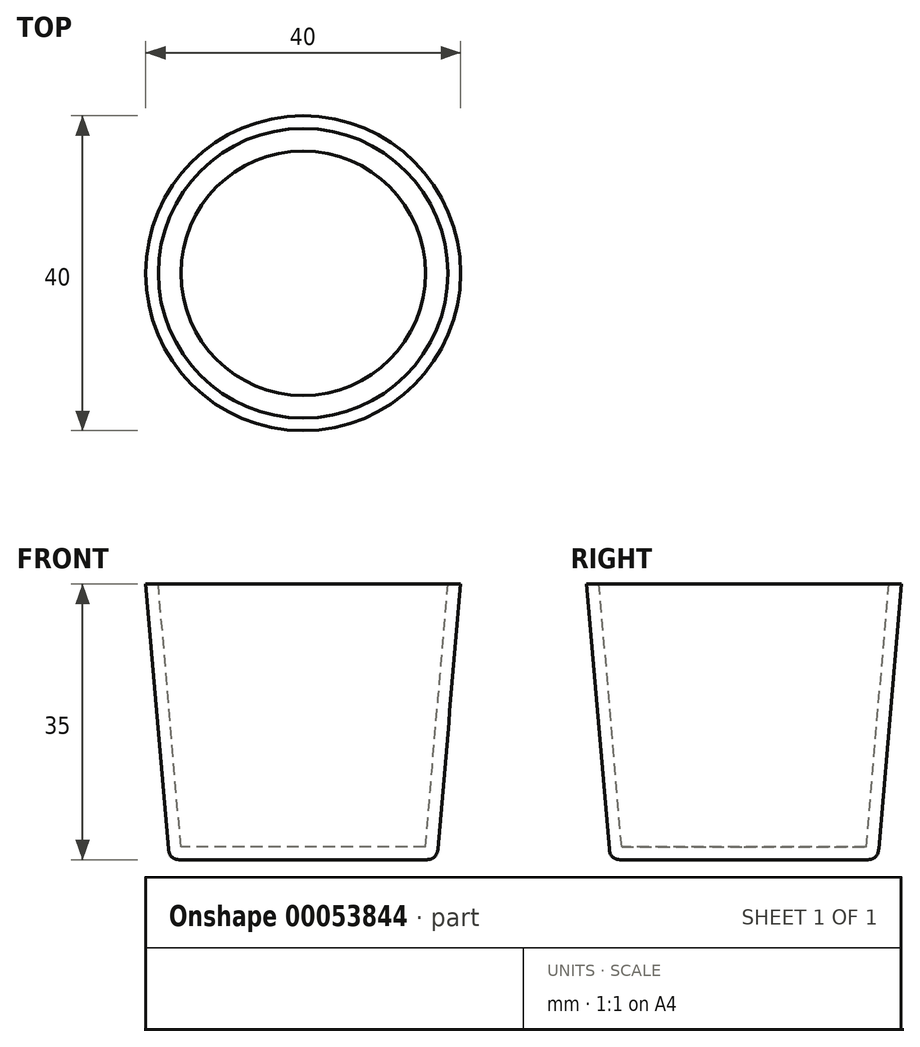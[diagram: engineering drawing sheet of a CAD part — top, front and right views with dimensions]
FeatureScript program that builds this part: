
annotation { "Feature Type Name" : "Feature", "Feature Type Description" : "" }
export const myFeature = defineFeature(function(context is Context, id is Id, definition is map)
    precondition{}
    {
        {
            var Q0;
            Q0=qCreatedBy(makeId("Front.planeOp"),FACE);
            var sketch = newSketch(context, id + "F0", { "sketchPlane" : qUnion([Q0])});
            skLineSegment(sketch, "E0", {"start": v(0, 0) * mm, "end": v(17, 0) * mm});
            skLineSegment(sketch, "E1", {"start": v(17, 0) * mm, "end": v(20, 35) * mm});
            skLineSegment(sketch, "E2", {"start": v(20, 35) * mm, "end": v(0, 35) * mm});
            skLineSegment(sketch, "E3", {"start": v(0, 35) * mm, "end": v(0, 0) * mm});
            skSolve(sketch);
        }
        {
            var Q0;
            Q0=makeQuery(id+"F0.imprint","IMPRINT",FACE,{"disambiguationData":[TD([[makeQuery(id+"F0.imprint","IMPRINT",EDGE,{"derivedFrom":sQuery(id+"F0.wireOp",EDGE,"E0")}),1.0]])]});
            var Q1;
            Q1=sQuery(id+"F0.wireOp",EDGE,"E3");
            revolve(context, id + "F1", {"entities" : qUnion([Q0]), "axis" : qUnion([Q1]), "revolveType" : RevolveType.FULL});
        }
        {
            var Q0;
            Q0=makeQuery(id+"F1.opRevolve","SWEPT_FACE",FACE,{"disambiguationData":[OSD([sQuery(id+"F0.wireOp",EDGE,"E2")])]});
            shell(context, id + "F2", {"entities" : qUnion([Q0]), "thickness" : 1.6 * mm});
        }
        {
            var Q0;
            Q0=makeQuery(id+"F1.opRevolve","SWEPT_EDGE",EDGE,{"disambiguationData":[OSD([sQuery(id+"F0.wireOp",EDGE,"E0"),sQuery(id+"F0.wireOp",EDGE,"E1")])]});
            fillet(context, id + "F3", {"entities" : qUnion([Q0]), "radius" : 1.5 * mm, "tangentPropagation" : true, "rho" : 0.5, "crossSection" : FilletCrossSection.CONIC, "allowEdgeOverflow" : false});
        }
    });
